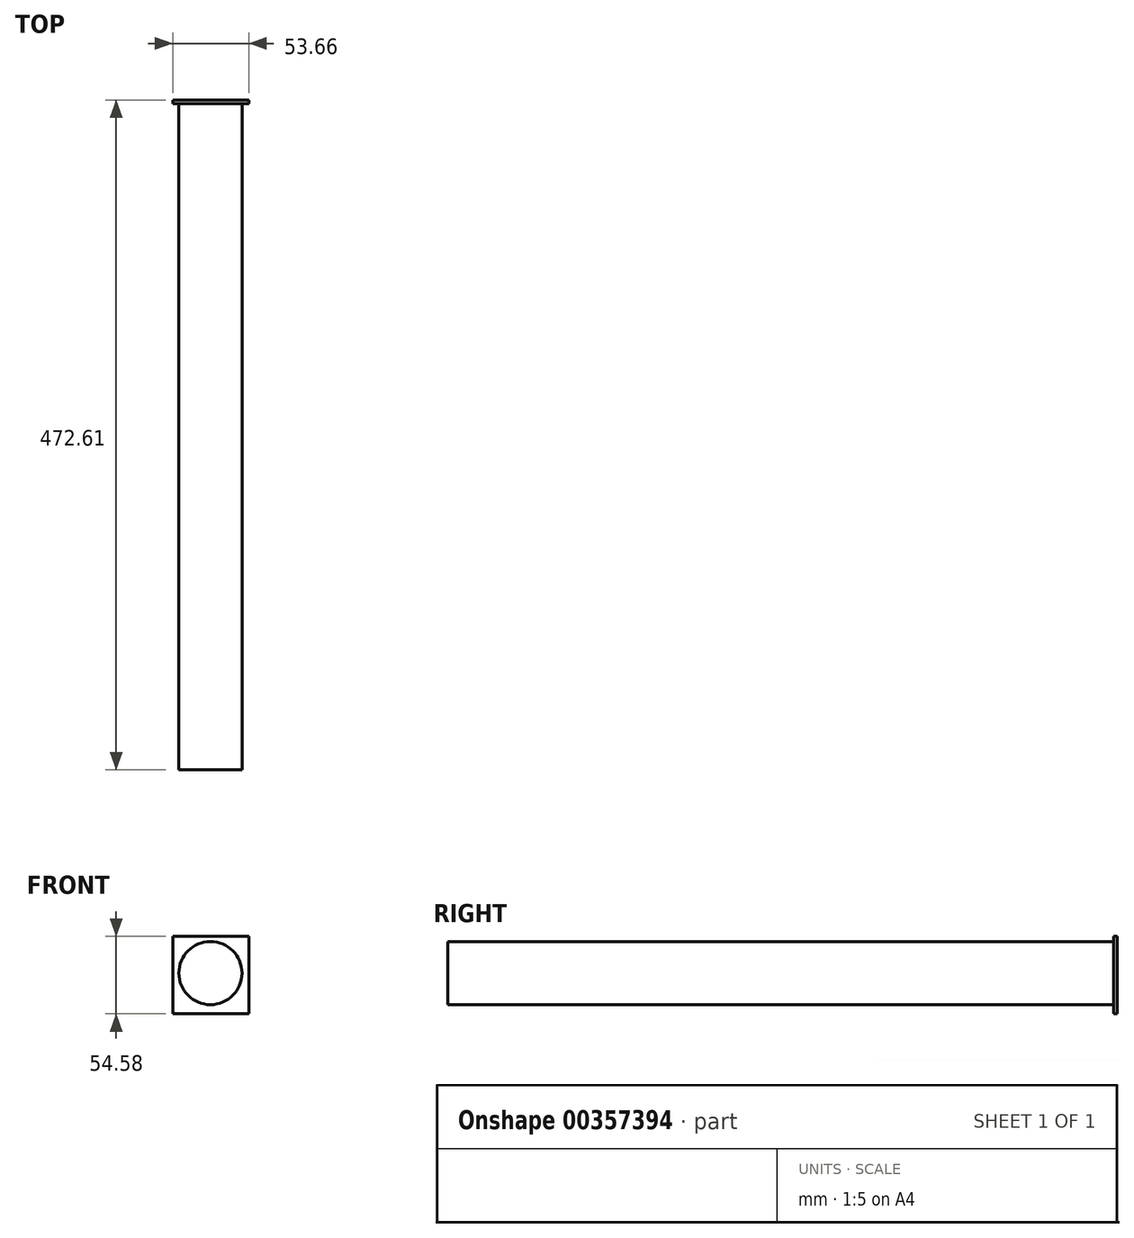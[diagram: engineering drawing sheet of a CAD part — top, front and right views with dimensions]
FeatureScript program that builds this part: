
annotation { "Feature Type Name" : "Feature", "Feature Type Description" : "" }
export const myFeature = defineFeature(function(context is Context, id is Id, definition is map)
    precondition{}
    {
        {
            var Q0;
            Q0=qCreatedBy(makeId("Front.planeOp"),FACE);
            var sketch = newSketch(context, id + "F0", { "sketchPlane" : qUnion([Q0])});
            skCircle(sketch, "E0", {"center": v(0, 0) * mm, "radius": 22.27 * mm});
            skSolve(sketch);
        }
        {
            var Q0;
            Q0=makeQuery(id+"F0.imprint","IMPRINT",FACE,{"disambiguationData":[TD([[makeQuery(id+"F0.imprint","IMPRINT",EDGE,{"derivedFrom":sQuery(id+"F0.wireOp",EDGE,"E0")}),1.0]])]});
            extrude(context, id + "F1", {"entities" : qUnion([Q0]), "depth" : 470 * mm});
        }
        {
            var Q0;
            Q0=qCreatedBy(makeId("Front.planeOp"),FACE);
            var sketch = newSketch(context, id + "F2", { "sketchPlane" : qUnion([Q0])});
            skLineSegment(sketch, "E1.bottom", {"start": v(27.07, 25.82) * mm, "end": v(-26.59, 25.82) * mm});
            skLineSegment(sketch, "E1.top", {"start": v(27.07, -28.76) * mm, "end": v(-26.59, -28.76) * mm});
            skLineSegment(sketch, "E1.left", {"start": v(27.07, 25.82) * mm, "end": v(27.07, -28.76) * mm});
            skLineSegment(sketch, "E1.right", {"start": v(-26.59, 25.82) * mm, "end": v(-26.59, -28.76) * mm});
            skSolve(sketch);
        }
        {
            var Q0;
            Q0=makeQuery(id+"F2.imprint","IMPRINT",FACE,{"disambiguationData":[TD([[makeQuery(id+"F2.imprint","IMPRINT",EDGE,{"derivedFrom":sQuery(id+"F2.wireOp",EDGE,"E1.bottom")}),1.0]])]});
            extrude(context, id + "F3", {"entities" : qUnion([Q0]), "operationType" : NewBodyOperationType.ADD, "oppositeDirection" : true, "depth" : 2.6 * mm});
        }
    });
